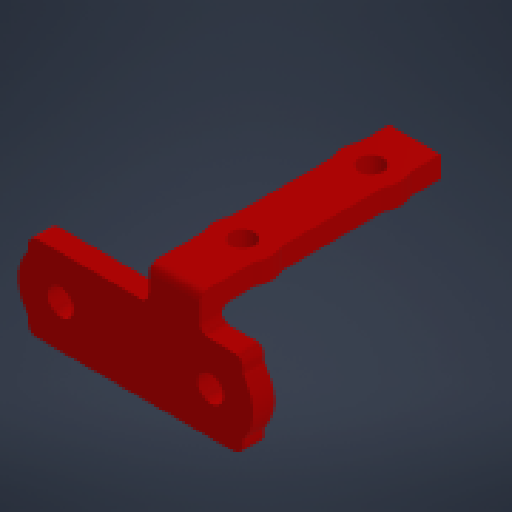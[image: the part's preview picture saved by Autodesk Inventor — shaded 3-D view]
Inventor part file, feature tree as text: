
AUTODESK INVENTOR PART (.ipt)
format: ipt  version: 2024.1 (Build 281209000, 209)  size: 293,376 bytes
history: native  units: in
note: dims shown in document units (in); Inventor stores cm internally (conversion verified against a paired STEP export)
features: extrude x5, sketch x5, projected_geometry x5, other x3, reference x2, direct_edit x1, imported_body x1
ambient origin geometry x8: Origin, YZ Plane, XZ Plane, XY Plane, X Axis, Y Axis, Z Axis, Center Point
bodies: Solid1 (feature_tree)
feature tree (22):
  direct_edit  "Direct Edit1"
  extrude  "Extrusion1"  Depth=0.3937in TaperAngle=0.0deg
  extrude  "Extrusion2"  Depth=11.811in
  extrude  "Extrusion3"  Depth=0.3937in TaperAngle=0.0deg
  extrude  "Extrusion4"  Depth=0.3937in TaperAngle=0.0deg
  extrude  "Extrusion5"  [1 undecoded]
  sketch  "Sketch1"  dims[d0=8.7087in d1=0.3937in d2=0.3937in d3=0.3937in d4=0.0in]
  projected_geometry  "Projected Loop1"
  sketch  "Sketch2"  dims[d5=11.811in d6=11.811in]
  projected_geometry  "Projected Loop2"
  sketch  "Sketch3"  dims[d7=0.3937in d8=0.0in d9=0.3937in d10=0.0in]
  projected_geometry  "Projected Loop3"
  reference  "Reference1"
  sketch  "Sketch4"  dims[d11=0.3937in d12=0.0in d13=0.3937in d14=0.0in]
  reference  "Reference2"
  projected_geometry  "Projected Loop4"
  sketch  "Sketch5"
  projected_geometry  "Projected Loop5"
  imported_body  "Base1"
  other  "Scale1"
  other  "EnsambleGripper.iam"
  other  "Gripper:1"
note: 1 required parameter value undecoded (feature->parameter linkage not recoverable at this tier; creation-order binding heuristic only, values carry confidence <= 0.55)
